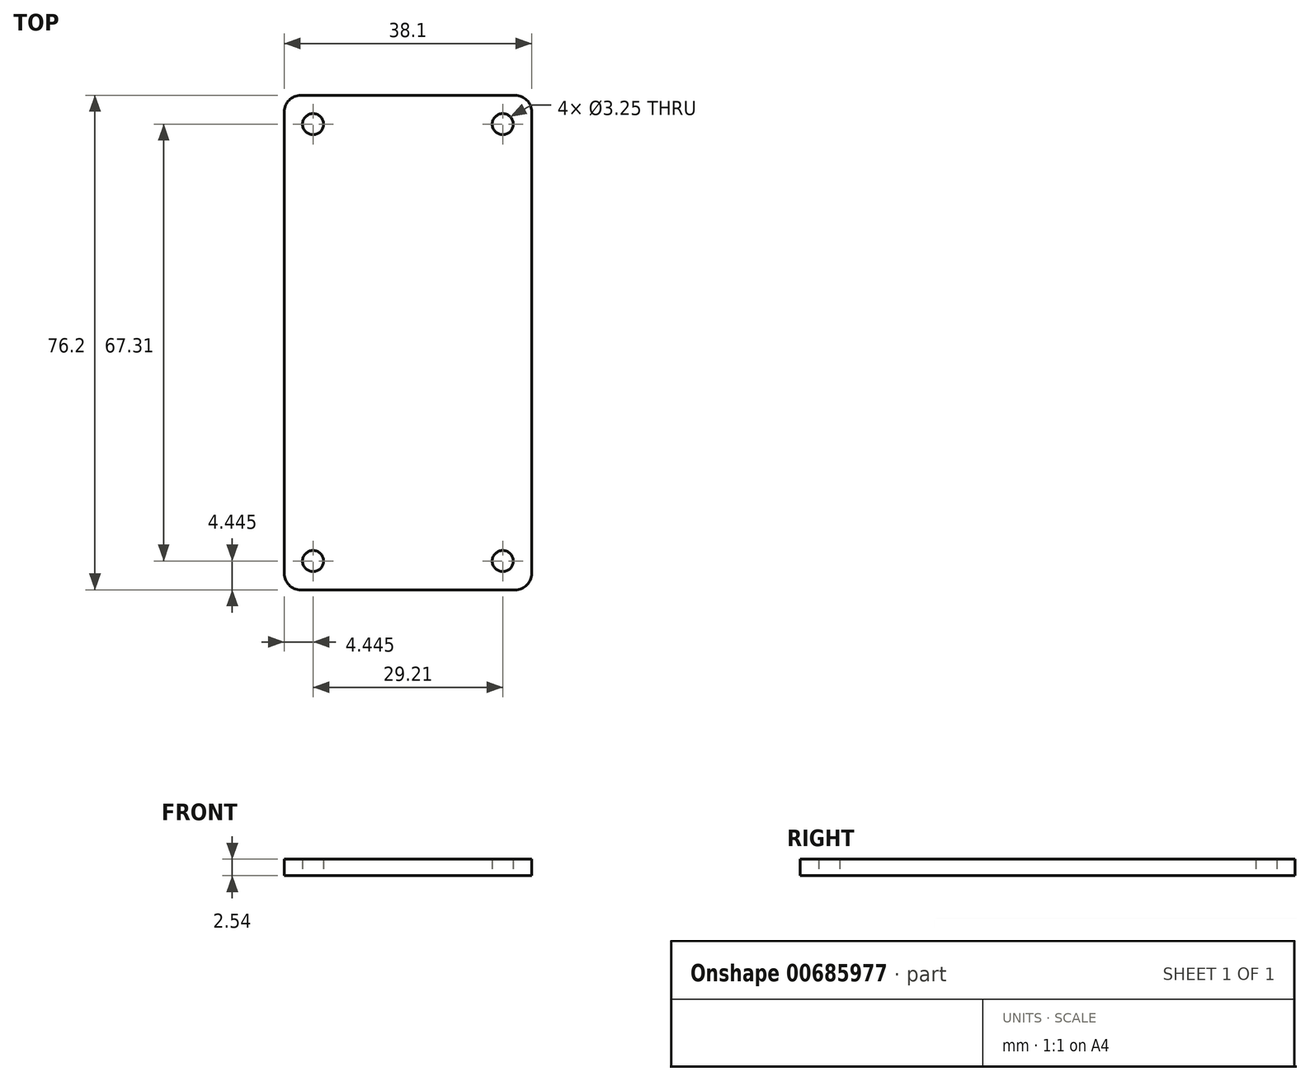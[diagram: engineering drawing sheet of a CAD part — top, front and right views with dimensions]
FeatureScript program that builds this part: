
annotation { "Feature Type Name" : "Feature", "Feature Type Description" : "" }
export const myFeature = defineFeature(function(context is Context, id is Id, definition is map)
    precondition{}
    {
        {
            var Q0;
            Q0=qCreatedBy(makeId("Top.planeOp"),FACE);
            var sketch = newSketch(context, id + "F0", { "sketchPlane" : qUnion([Q0])});
            skLineSegment(sketch, "E0.bottom", {"start": v(-19.05, 38.1) * mm, "end": v(19.05, 38.1) * mm});
            skLineSegment(sketch, "E0.top", {"start": v(-19.05, -38.1) * mm, "end": v(19.05, -38.1) * mm});
            skLineSegment(sketch, "E0.left", {"start": v(-19.05, 38.1) * mm, "end": v(-19.05, -38.1) * mm});
            skLineSegment(sketch, "E0.right", {"start": v(19.05, 38.1) * mm, "end": v(19.05, -38.1) * mm});
            skPoint(sketch, "E0.middle", {"position": v(0, 0) * mm});
            skPoint(sketch, "E1", {"position": v(-14.6, 33.66) * mm});
            skPoint(sketch, "E2", {"position": v(14.6, 33.66) * mm});
            skPoint(sketch, "E3", {"position": v(14.6, -33.65) * mm});
            skPoint(sketch, "E4", {"position": v(-14.6, -33.65) * mm});
            skSolve(sketch);
        }
        {
            var Q0;
            Q0=makeQuery(id+"F0.imprint","IMPRINT",FACE,{"disambiguationData":[TD([[makeQuery(id+"F0.imprint","IMPRINT",EDGE,{"derivedFrom":sQuery(id+"F0.wireOp",EDGE,"E0.bottom")}),-1.0]])]});
            extrude(context, id + "F1", {"entities" : qUnion([Q0]), "depth" : 2.54 * mm, "offsetDistance" : 25.4 * mm});
        }
        {
            var Q0;
            Q0=sQuery(id+"F0.wireOp",VERTEX,"E1");
            var Q1;
            Q1=sQuery(id+"F0.wireOp",VERTEX,"E2");
            var Q2;
            Q2=sQuery(id+"F0.wireOp",VERTEX,"E3");
            var Q3;
            Q3=sQuery(id+"F0.wireOp",VERTEX,"E4");
            var Q4;
            Q4=makeQuery(id+"F1.opExtrude","SWEPT_BODY",BODY,{"disambiguationData":[OSD([sQuery(id+"F0.wireOp",EDGE,"E0.bottom"),sQuery(id+"F0.wireOp",EDGE,"E0.top"),sQuery(id+"F0.wireOp",EDGE,"E0.left"),sQuery(id+"F0.wireOp",EDGE,"E0.right")])]});
            hole(context, id + "F2", {"style" : HoleStyle.SIMPLE, "endStyle" : HoleEndStyle.BLIND, "oppositeDirection" : true, "standardTappedOrClearance" : lookupTablePath({ "fit" : "Normal (ASME)", "standard" : "ANSI", "size" : "#4", "type" : "Clearance" }), "standardBlindInLast" : lookupTablePath({ "fit" : "Normal", "standard" : "ANSI", "engagement" : "75%", "pitch" : "40 tpi", "size" : "#4", "type" : "Clearance & tapped" }), "holeDiameter" : 3.25 * mm, "majorDiameter" : 2.84 * mm, "holeDepth" : 14.6 * mm, "isTappedThrough" : true, "tappedDepth" : 12.7 * mm, "tapClearance" : 3, "startFromSketch" : true, "locations" : qUnion([Q0, Q1, Q2, Q3]), "scope" : qUnion([Q4])});
        }
        {
            var Q0;
            Q0=makeQuery(id+"F1.opExtrude","SWEPT_EDGE",EDGE,{"disambiguationData":[OSD([sQuery(id+"F0.wireOp",EDGE,"E0.bottom"),sQuery(id+"F0.wireOp",EDGE,"E0.left")])]});
            var Q1;
            Q1=makeQuery(id+"F1.opExtrude","SWEPT_EDGE",EDGE,{"disambiguationData":[OSD([sQuery(id+"F0.wireOp",EDGE,"E0.top"),sQuery(id+"F0.wireOp",EDGE,"E0.left")])]});
            var Q2;
            Q2=makeQuery(id+"F1.opExtrude","SWEPT_EDGE",EDGE,{"disambiguationData":[OSD([sQuery(id+"F0.wireOp",EDGE,"E0.bottom"),sQuery(id+"F0.wireOp",EDGE,"E0.right")])]});
            var Q3;
            Q3=makeQuery(id+"F1.opExtrude","SWEPT_EDGE",EDGE,{"disambiguationData":[OSD([sQuery(id+"F0.wireOp",EDGE,"E0.top"),sQuery(id+"F0.wireOp",EDGE,"E0.right")])]});
            fillet(context, id + "F3", {"entities" : qUnion([Q0, Q1, Q2, Q3]), "radius" : 2.54 * mm, "tangentPropagation" : true, "allowEdgeOverflow" : false});
        }
    });
